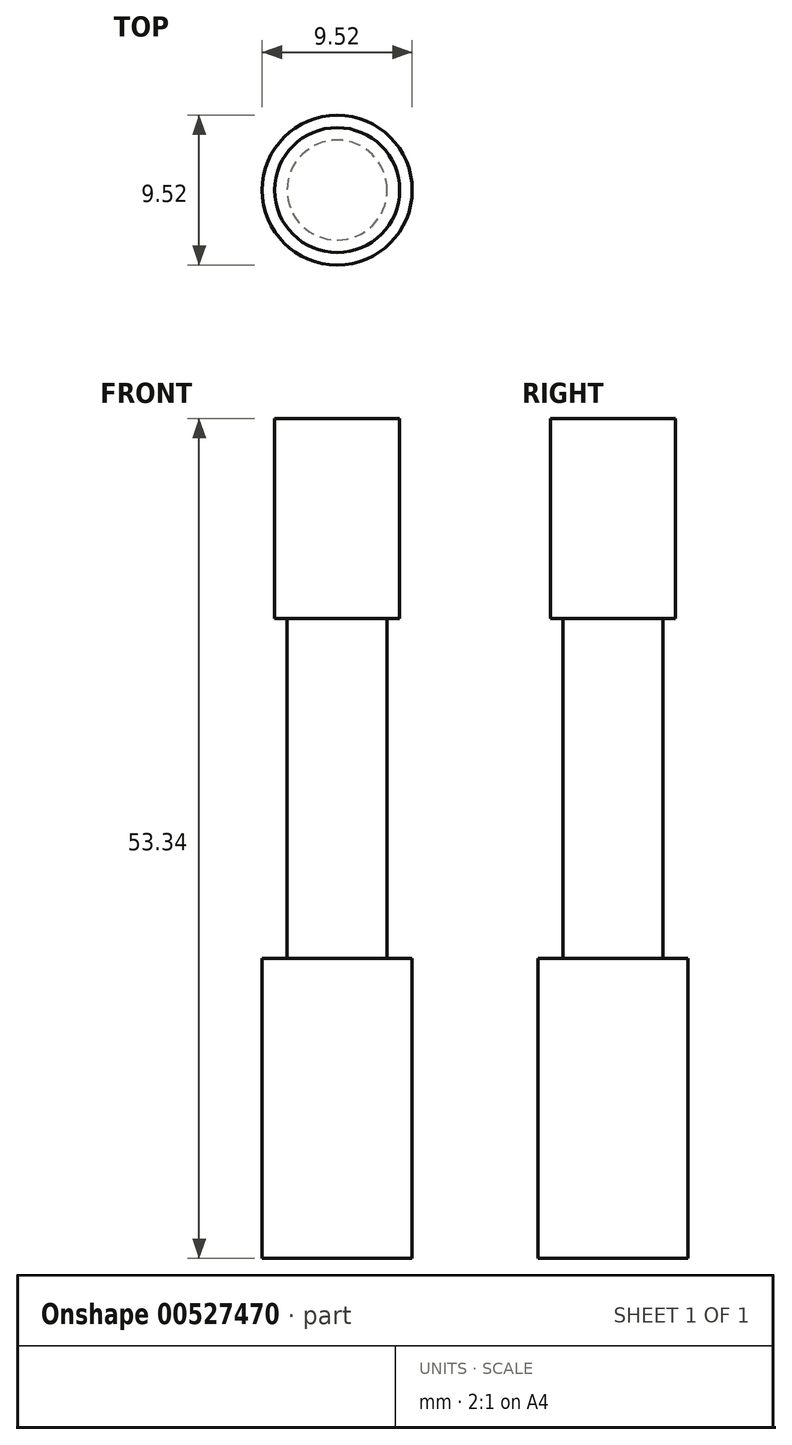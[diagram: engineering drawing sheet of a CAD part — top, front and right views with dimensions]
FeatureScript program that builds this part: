
annotation { "Feature Type Name" : "Feature", "Feature Type Description" : "" }
export const myFeature = defineFeature(function(context is Context, id is Id, definition is map)
    precondition{}
    {
        {
            var Q0;
            Q0=qCreatedBy(makeId("Top.planeOp"),FACE);
            var sketch = newSketch(context, id + "F0", { "sketchPlane" : qUnion([Q0])});
            skCircle(sketch, "E0", {"center": v(0, 0) * mm, "radius": 4.76 * mm});
            skSolve(sketch);
        }
        {
            var Q0;
            Q0=makeQuery(id+"F0.imprint","IMPRINT",FACE,{"disambiguationData":[TD([[makeQuery(id+"F0.imprint","IMPRINT",EDGE,{"derivedFrom":sQuery(id+"F0.wireOp",EDGE,"E0")}),1.0]])]});
            extrude(context, id + "F1", {"entities" : qUnion([Q0]), "depth" : 19.05 * mm, "offsetDistance" : 25.4 * mm});
        }
        {
            var Q0;
            Q0=makeQuery(id+"F1.opExtrude","CAP_FACE",FACE,{"disambiguationData":[OSD([sQuery(id+"F0.wireOp",EDGE,"E0")])],"isStart":false});
            var sketch = newSketch(context, id + "F2", { "sketchPlane" : qUnion([Q0])});
            skCircle(sketch, "E1", {"center": v(0, 0) * mm, "radius": 3.18 * mm});
            skSolve(sketch);
        }
        {
            var Q0;
            Q0=qSketchRegion(id+"F2",true);
            extrude(context, id + "F3", {"entities" : qUnion([Q0]), "operationType" : NewBodyOperationType.ADD, "depth" : 21.59 * mm, "offsetDistance" : 25.4 * mm});
        }
        {
            var Q0;
            Q0=makeQuery(id+"F3.opExtrude","CAP_FACE",FACE,{"disambiguationData":[OSD([sQuery(id+"F2.wireOp",EDGE,"E1")])],"isStart":false});
            var sketch = newSketch(context, id + "F4", { "sketchPlane" : qUnion([Q0])});
            skCircle(sketch, "E2", {"center": v(0, 0) * mm, "radius": 3.97 * mm});
            skSolve(sketch);
        }
        {
            var Q0;
            Q0=qSketchRegion(id+"F4",true);
            extrude(context, id + "F5", {"entities" : qUnion([Q0]), "operationType" : NewBodyOperationType.ADD, "depth" : 12.7 * mm, "offsetDistance" : 25.4 * mm});
        }
    });
